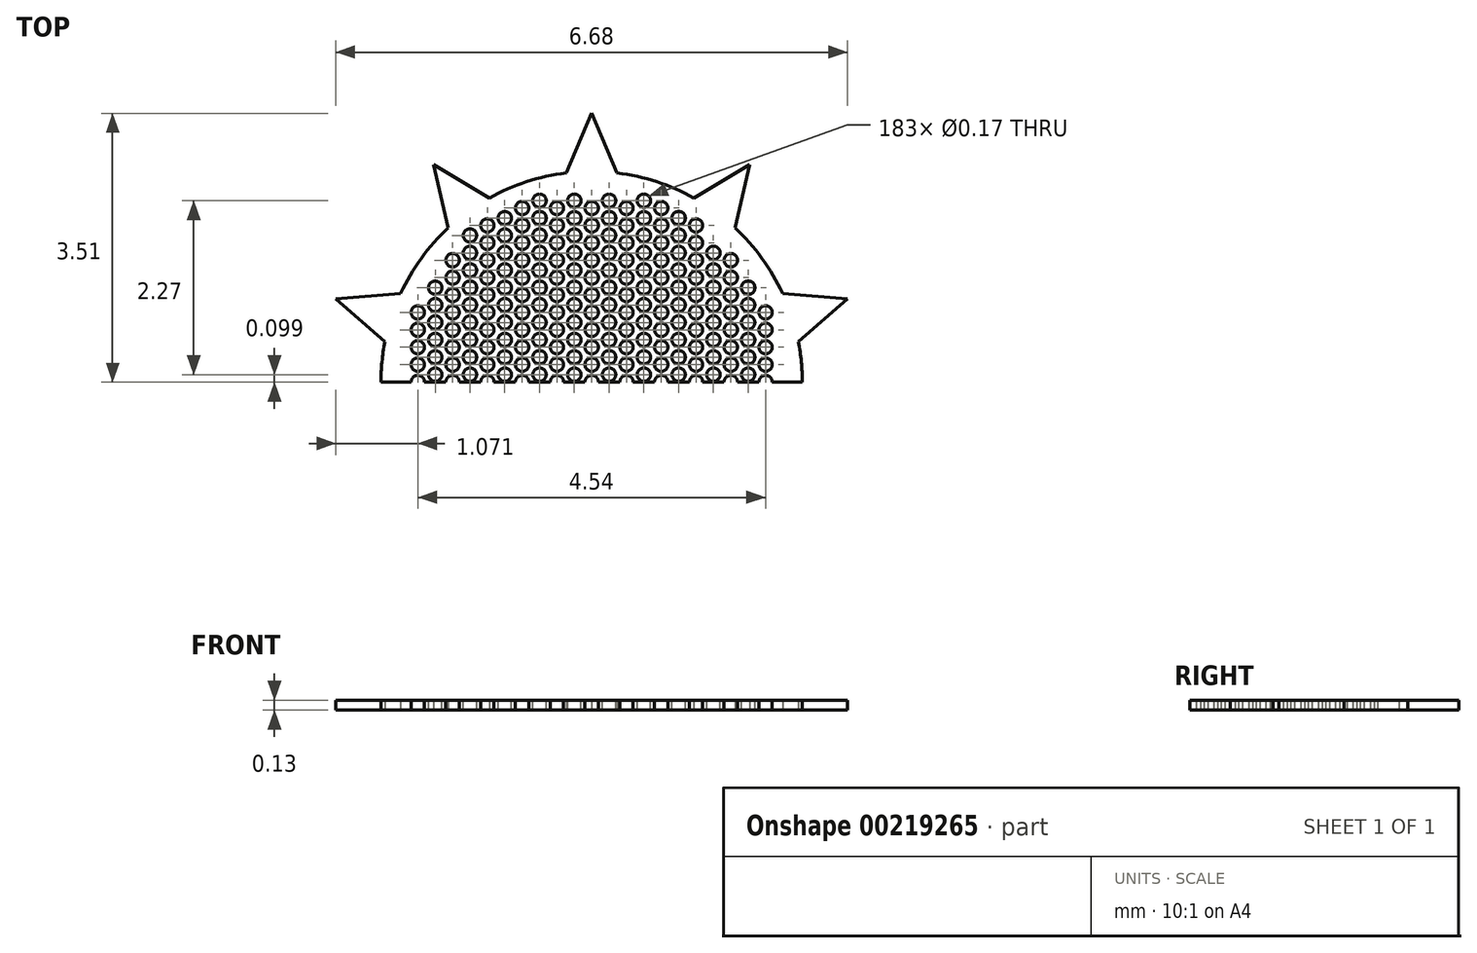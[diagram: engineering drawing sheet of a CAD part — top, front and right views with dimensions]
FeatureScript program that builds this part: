
annotation { "Feature Type Name" : "Feature", "Feature Type Description" : "" }
export const myFeature = defineFeature(function(context is Context, id is Id, definition is map)
    precondition{}
    {
        {
            var Q0;
            Q0=qCreatedBy(makeId("Top.planeOp"),FACE);
            var sketch = newSketch(context, id + "F0", { "sketchPlane" : qUnion([Q0])});
            skCircle(sketch, "E0", {"center": v(0, 0) * mm, "radius": 2.5 * mm});
            skCircle(sketch, "E1", {"center": v(0, 0) * mm, "radius": 2.75 * mm});
            skPoint(sketch, "E2", {"position": v(0, 2.75) * mm});
            skLineSegment(sketch, "E3", {"start": v(-3.94, 3.51) * mm, "end": v(3.7, 3.51) * mm, "construction": true});
            skLineSegment(sketch, "E4", {"start": v(0, 3.51) * mm, "end": v(-0.33, 2.73) * mm});
            skLineSegment(sketch, "E5", {"start": v(0, 3.51) * mm, "end": v(0.33, 2.73) * mm});
            skLineSegment(sketch, "E6.1.0", {"start": v(-2.06, 2.84) * mm, "end": v(-1.87, 2.01) * mm});
            skLineSegment(sketch, "E6.1.1", {"start": v(-2.06, 2.84) * mm, "end": v(-1.34, 2.4) * mm});
            skLineSegment(sketch, "E6.2.0", {"start": v(-3.34, 1.09) * mm, "end": v(-2.7, 0.53) * mm});
            skLineSegment(sketch, "E6.2.1", {"start": v(-3.34, 1.09) * mm, "end": v(-2.5, 1.16) * mm});
            skLineSegment(sketch, "E6.3.0", {"start": v(-3.34, -1.09) * mm, "end": v(-2.5, -1.16) * mm});
            skLineSegment(sketch, "E6.3.1", {"start": v(-3.34, -1.09) * mm, "end": v(-2.7, -0.53) * mm});
            skLineSegment(sketch, "E6.4.0", {"start": v(-2.06, -2.84) * mm, "end": v(-1.34, -2.4) * mm});
            skLineSegment(sketch, "E6.4.1", {"start": v(-2.06, -2.84) * mm, "end": v(-1.87, -2.01) * mm});
            skLineSegment(sketch, "E6.5.0", {"start": v(0, -3.51) * mm, "end": v(0.33, -2.73) * mm});
            skLineSegment(sketch, "E6.5.1", {"start": v(0, -3.51) * mm, "end": v(-0.33, -2.73) * mm});
            skLineSegment(sketch, "E6.6.0", {"start": v(2.06, -2.84) * mm, "end": v(1.87, -2.01) * mm});
            skLineSegment(sketch, "E6.6.1", {"start": v(2.06, -2.84) * mm, "end": v(1.34, -2.4) * mm});
            skLineSegment(sketch, "E6.7.0", {"start": v(3.34, -1.09) * mm, "end": v(2.7, -0.53) * mm});
            skLineSegment(sketch, "E6.7.1", {"start": v(3.34, -1.09) * mm, "end": v(2.5, -1.16) * mm});
            skLineSegment(sketch, "E6.8.0", {"start": v(3.34, 1.09) * mm, "end": v(2.5, 1.16) * mm});
            skLineSegment(sketch, "E6.8.1", {"start": v(3.34, 1.09) * mm, "end": v(2.7, 0.53) * mm});
            skLineSegment(sketch, "E6.9.0", {"start": v(2.06, 2.84) * mm, "end": v(1.34, 2.4) * mm});
            skLineSegment(sketch, "E6.9.1", {"start": v(2.06, 2.84) * mm, "end": v(1.87, 2.01) * mm});
            skSolve(sketch);
        }
        {
            var Q0;
            Q0=qSketchRegion(id+"F0",true);
            var Q1;
            Q1=makeQuery(id+"F0.imprint","IMPRINT",FACE,{"disambiguationData":[TD([[makeQuery(id+"F0.imprint","IMPRINT",EDGE,{"derivedFrom":sQuery(id+"F0.wireOp",EDGE,"E0")}),1.0]])]});
            extrude(context, id + "F1", {"entities" : qUnion([Q0, Q1]), "depth" : 0.13 * mm});
        }
        {
            var Q0;
            Q0=makeQuery(id+"F1.opExtrude","CAP_FACE",FACE,{"disambiguationData":[OSD([sQuery(id+"F0.wireOp",EDGE,"E1"),sQuery(id+"F0.wireOp",EDGE,"E4"),sQuery(id+"F0.wireOp",EDGE,"E5"),sQuery(id+"F0.wireOp",EDGE,"E6.1.0"),sQuery(id+"F0.wireOp",EDGE,"E6.1.1"),sQuery(id+"F0.wireOp",EDGE,"E6.2.0"),sQuery(id+"F0.wireOp",EDGE,"E6.2.1"),sQuery(id+"F0.wireOp",EDGE,"E6.3.0"),sQuery(id+"F0.wireOp",EDGE,"E6.3.1"),sQuery(id+"F0.wireOp",EDGE,"E6.4.0"),sQuery(id+"F0.wireOp",EDGE,"E6.4.1"),sQuery(id+"F0.wireOp",EDGE,"E6.5.0"),sQuery(id+"F0.wireOp",EDGE,"E6.5.1"),sQuery(id+"F0.wireOp",EDGE,"E6.6.0"),sQuery(id+"F0.wireOp",EDGE,"E6.6.1"),sQuery(id+"F0.wireOp",EDGE,"E6.7.0"),sQuery(id+"F0.wireOp",EDGE,"E6.7.1"),sQuery(id+"F0.wireOp",EDGE,"E6.8.0"),sQuery(id+"F0.wireOp",EDGE,"E6.8.1"),sQuery(id+"F0.wireOp",EDGE,"E6.9.0"),sQuery(id+"F0.wireOp",EDGE,"E6.9.1")])],"isStart":false});
            cPlane(context, id + "F2", {"entities" : qUnion([Q0]), "cplaneType" : CPlaneType.OFFSET, "offset" : 0 * mm, "width" : 150 * mm, "height" : 150 * mm});
        }
        {
            var Q0;
            Q0=qCreatedBy(id+"F2.planeOp",FACE);
            var sketch = newSketch(context, id + "F3", { "sketchPlane" : qUnion([Q0])});
            skCircle(sketch, "E7.2.1.8", {"center": v(-2.04, 1.23) * mm, "radius": 0.09 * mm});
            skCircle(sketch, "E7.2.1.9", {"center": v(-2.04, 1) * mm, "radius": 0.09 * mm});
            skCircle(sketch, "E7.0.1.10", {"center": v(-2.27, 0.91) * mm, "radius": 0.09 * mm});
            skCircle(sketch, "E7.2.1.10", {"center": v(-2.04, 0.78) * mm, "radius": 0.09 * mm});
            skCircle(sketch, "E7.2.2.5", {"center": v(-1.59, 1.91) * mm, "radius": 0.09 * mm});
            skCircle(sketch, "E7.2.2.6", {"center": v(-1.59, 1.69) * mm, "radius": 0.09 * mm});
            skCircle(sketch, "E7.0.2.7", {"center": v(-1.82, 1.6) * mm, "radius": 0.09 * mm});
            skCircle(sketch, "E7.2.2.7", {"center": v(-1.59, 1.46) * mm, "radius": 0.09 * mm});
            skCircle(sketch, "E7.0.2.8", {"center": v(-1.82, 1.36) * mm, "radius": 0.09 * mm});
            skCircle(sketch, "E7.2.2.8", {"center": v(-1.59, 1.23) * mm, "radius": 0.09 * mm});
            skCircle(sketch, "E7.0.2.9", {"center": v(-1.82, 1.14) * mm, "radius": 0.09 * mm});
            skCircle(sketch, "E7.2.2.9", {"center": v(-1.59, 1) * mm, "radius": 0.09 * mm});
            skCircle(sketch, "E7.0.2.10", {"center": v(-1.82, 0.91) * mm, "radius": 0.09 * mm});
            skCircle(sketch, "E7.2.2.10", {"center": v(-1.59, 0.78) * mm, "radius": 0.09 * mm});
            skCircle(sketch, "E7.2.3.4", {"center": v(-1.13, 2.14) * mm, "radius": 0.09 * mm});
            skCircle(sketch, "E7.0.3.5", {"center": v(-1.36, 2.05) * mm, "radius": 0.09 * mm});
            skCircle(sketch, "E7.2.3.5", {"center": v(-1.13, 1.91) * mm, "radius": 0.09 * mm});
            skCircle(sketch, "E7.0.3.6", {"center": v(-1.36, 1.82) * mm, "radius": 0.09 * mm});
            skCircle(sketch, "E7.2.3.6", {"center": v(-1.13, 1.69) * mm, "radius": 0.09 * mm});
            skCircle(sketch, "E7.0.3.7", {"center": v(-1.36, 1.6) * mm, "radius": 0.09 * mm});
            skCircle(sketch, "E7.2.3.7", {"center": v(-1.13, 1.46) * mm, "radius": 0.09 * mm});
            skCircle(sketch, "E7.0.3.8", {"center": v(-1.36, 1.36) * mm, "radius": 0.09 * mm});
            skCircle(sketch, "E7.2.3.8", {"center": v(-1.13, 1.23) * mm, "radius": 0.09 * mm});
            skCircle(sketch, "E7.0.3.9", {"center": v(-1.36, 1.14) * mm, "radius": 0.09 * mm});
            skCircle(sketch, "E7.2.3.9", {"center": v(-1.13, 1) * mm, "radius": 0.09 * mm});
            skCircle(sketch, "E7.0.3.10", {"center": v(-1.36, 0.91) * mm, "radius": 0.09 * mm});
            skCircle(sketch, "E7.2.3.10", {"center": v(-1.13, 0.78) * mm, "radius": 0.09 * mm});
            skCircle(sketch, "E7.2.4.3", {"center": v(-0.68, 2.37) * mm, "radius": 0.09 * mm});
            skCircle(sketch, "E7.0.4.4", {"center": v(-0.9, 2.27) * mm, "radius": 0.09 * mm});
            skCircle(sketch, "E7.2.4.4", {"center": v(-0.68, 2.14) * mm, "radius": 0.09 * mm});
            skCircle(sketch, "E7.0.4.5", {"center": v(-0.9, 2.05) * mm, "radius": 0.09 * mm});
            skCircle(sketch, "E7.2.4.5", {"center": v(-0.68, 1.91) * mm, "radius": 0.09 * mm});
            skCircle(sketch, "E7.0.4.6", {"center": v(-0.9, 1.82) * mm, "radius": 0.09 * mm});
            skCircle(sketch, "E7.2.4.6", {"center": v(-0.68, 1.69) * mm, "radius": 0.09 * mm});
            skCircle(sketch, "E7.0.4.7", {"center": v(-0.9, 1.6) * mm, "radius": 0.09 * mm});
            skCircle(sketch, "E7.2.4.7", {"center": v(-0.68, 1.46) * mm, "radius": 0.09 * mm});
            skCircle(sketch, "E7.0.4.8", {"center": v(-0.9, 1.36) * mm, "radius": 0.09 * mm});
            skCircle(sketch, "E7.2.4.8", {"center": v(-0.68, 1.23) * mm, "radius": 0.09 * mm});
            skCircle(sketch, "E7.0.4.9", {"center": v(-0.9, 1.14) * mm, "radius": 0.09 * mm});
            skCircle(sketch, "E7.2.4.9", {"center": v(-0.68, 1) * mm, "radius": 0.09 * mm});
            skCircle(sketch, "E7.0.4.10", {"center": v(-0.9, 0.91) * mm, "radius": 0.09 * mm});
            skCircle(sketch, "E7.2.4.10", {"center": v(-0.68, 0.78) * mm, "radius": 0.09 * mm});
            skCircle(sketch, "E7.2.5.3", {"center": v(-0.23, 2.37) * mm, "radius": 0.09 * mm});
            skCircle(sketch, "E7.0.5.4", {"center": v(-0.45, 2.27) * mm, "radius": 0.09 * mm});
            skCircle(sketch, "E7.2.5.4", {"center": v(-0.23, 2.14) * mm, "radius": 0.09 * mm});
            skCircle(sketch, "E7.0.5.5", {"center": v(-0.45, 2.05) * mm, "radius": 0.09 * mm});
            skCircle(sketch, "E7.2.5.5", {"center": v(-0.23, 1.91) * mm, "radius": 0.09 * mm});
            skCircle(sketch, "E7.0.5.6", {"center": v(-0.45, 1.82) * mm, "radius": 0.09 * mm});
            skCircle(sketch, "E7.2.5.6", {"center": v(-0.23, 1.69) * mm, "radius": 0.09 * mm});
            skCircle(sketch, "E7.0.5.7", {"center": v(-0.45, 1.6) * mm, "radius": 0.09 * mm});
            skCircle(sketch, "E7.2.5.7", {"center": v(-0.23, 1.46) * mm, "radius": 0.09 * mm});
            skCircle(sketch, "E7.0.5.8", {"center": v(-0.45, 1.36) * mm, "radius": 0.09 * mm});
            skCircle(sketch, "E7.2.5.8", {"center": v(-0.23, 1.23) * mm, "radius": 0.09 * mm});
            skCircle(sketch, "E7.0.5.9", {"center": v(-0.45, 1.14) * mm, "radius": 0.09 * mm});
            skCircle(sketch, "E7.2.5.9", {"center": v(-0.23, 1) * mm, "radius": 0.09 * mm});
            skCircle(sketch, "E7.0.5.10", {"center": v(-0.45, 0.91) * mm, "radius": 0.09 * mm});
            skCircle(sketch, "E7.2.5.10", {"center": v(-0.23, 0.78) * mm, "radius": 0.09 * mm});
            skCircle(sketch, "E7.2.6.3", {"center": v(0.23, 2.37) * mm, "radius": 0.09 * mm});
            skCircle(sketch, "E7.0.6.4", {"center": v(0, 2.27) * mm, "radius": 0.09 * mm});
            skCircle(sketch, "E7.2.6.4", {"center": v(0.23, 2.14) * mm, "radius": 0.09 * mm});
            skCircle(sketch, "E7.0.6.5", {"center": v(0, 2.05) * mm, "radius": 0.09 * mm});
            skCircle(sketch, "E7.2.6.5", {"center": v(0.23, 1.91) * mm, "radius": 0.09 * mm});
            skCircle(sketch, "E7.0.6.6", {"center": v(0, 1.82) * mm, "radius": 0.09 * mm});
            skCircle(sketch, "E7.2.6.6", {"center": v(0.23, 1.69) * mm, "radius": 0.09 * mm});
            skCircle(sketch, "E7.0.6.7", {"center": v(0, 1.6) * mm, "radius": 0.09 * mm});
            skCircle(sketch, "E7.2.6.7", {"center": v(0.23, 1.46) * mm, "radius": 0.09 * mm});
            skCircle(sketch, "E7.0.6.8", {"center": v(0, 1.36) * mm, "radius": 0.09 * mm});
            skCircle(sketch, "E7.2.6.8", {"center": v(0.23, 1.23) * mm, "radius": 0.09 * mm});
            skCircle(sketch, "E7.0.6.9", {"center": v(0, 1.14) * mm, "radius": 0.09 * mm});
            skCircle(sketch, "E7.2.6.9", {"center": v(0.23, 1) * mm, "radius": 0.09 * mm});
            skCircle(sketch, "E7.0.6.10", {"center": v(0, 0.91) * mm, "radius": 0.09 * mm});
            skCircle(sketch, "E7.2.6.10", {"center": v(0.23, 0.78) * mm, "radius": 0.09 * mm});
            skCircle(sketch, "E7.2.7.3", {"center": v(0.68, 2.37) * mm, "radius": 0.09 * mm});
            skCircle(sketch, "E7.0.7.4", {"center": v(0.45, 2.27) * mm, "radius": 0.09 * mm});
            skCircle(sketch, "E7.2.7.4", {"center": v(0.68, 2.14) * mm, "radius": 0.09 * mm});
            skCircle(sketch, "E7.0.7.5", {"center": v(0.45, 2.05) * mm, "radius": 0.09 * mm});
            skCircle(sketch, "E7.2.7.5", {"center": v(0.68, 1.91) * mm, "radius": 0.09 * mm});
            skCircle(sketch, "E7.0.7.6", {"center": v(0.45, 1.82) * mm, "radius": 0.09 * mm});
            skCircle(sketch, "E7.2.7.6", {"center": v(0.68, 1.69) * mm, "radius": 0.09 * mm});
            skCircle(sketch, "E7.0.7.7", {"center": v(0.45, 1.6) * mm, "radius": 0.09 * mm});
            skCircle(sketch, "E7.2.7.7", {"center": v(0.68, 1.46) * mm, "radius": 0.09 * mm});
            skCircle(sketch, "E7.0.7.8", {"center": v(0.45, 1.36) * mm, "radius": 0.09 * mm});
            skCircle(sketch, "E7.2.7.8", {"center": v(0.68, 1.23) * mm, "radius": 0.09 * mm});
            skCircle(sketch, "E7.0.7.9", {"center": v(0.45, 1.14) * mm, "radius": 0.09 * mm});
            skCircle(sketch, "E7.2.7.9", {"center": v(0.68, 1) * mm, "radius": 0.09 * mm});
            skCircle(sketch, "E7.0.7.10", {"center": v(0.45, 0.91) * mm, "radius": 0.09 * mm});
            skCircle(sketch, "E7.2.7.10", {"center": v(0.68, 0.78) * mm, "radius": 0.09 * mm});
            skCircle(sketch, "E7.0.8.4", {"center": v(0.9, 2.27) * mm, "radius": 0.09 * mm});
            skCircle(sketch, "E7.2.8.4", {"center": v(1.14, 2.14) * mm, "radius": 0.09 * mm});
            skCircle(sketch, "E7.0.8.5", {"center": v(0.9, 2.05) * mm, "radius": 0.09 * mm});
            skCircle(sketch, "E7.2.8.5", {"center": v(1.14, 1.91) * mm, "radius": 0.09 * mm});
            skCircle(sketch, "E7.0.8.6", {"center": v(0.9, 1.82) * mm, "radius": 0.09 * mm});
            skCircle(sketch, "E7.2.8.6", {"center": v(1.14, 1.69) * mm, "radius": 0.09 * mm});
            skCircle(sketch, "E7.0.8.7", {"center": v(0.9, 1.6) * mm, "radius": 0.09 * mm});
            skCircle(sketch, "E7.2.8.7", {"center": v(1.14, 1.46) * mm, "radius": 0.09 * mm});
            skCircle(sketch, "E7.0.8.8", {"center": v(0.9, 1.36) * mm, "radius": 0.09 * mm});
            skCircle(sketch, "E7.2.8.8", {"center": v(1.14, 1.23) * mm, "radius": 0.09 * mm});
            skCircle(sketch, "E7.0.8.9", {"center": v(0.9, 1.14) * mm, "radius": 0.09 * mm});
            skCircle(sketch, "E7.2.8.9", {"center": v(1.14, 1) * mm, "radius": 0.09 * mm});
            skCircle(sketch, "E7.0.8.10", {"center": v(0.9, 0.91) * mm, "radius": 0.09 * mm});
            skCircle(sketch, "E7.2.8.10", {"center": v(1.14, 0.78) * mm, "radius": 0.09 * mm});
            skCircle(sketch, "E7.0.9.5", {"center": v(1.36, 2.05) * mm, "radius": 0.09 * mm});
            skCircle(sketch, "E7.0.9.6", {"center": v(1.36, 1.82) * mm, "radius": 0.09 * mm});
            skCircle(sketch, "E7.2.9.6", {"center": v(1.6, 1.69) * mm, "radius": 0.09 * mm});
            skCircle(sketch, "E7.0.9.7", {"center": v(1.36, 1.6) * mm, "radius": 0.09 * mm});
            skCircle(sketch, "E7.2.9.7", {"center": v(1.6, 1.46) * mm, "radius": 0.09 * mm});
            skCircle(sketch, "E7.0.9.8", {"center": v(1.36, 1.36) * mm, "radius": 0.09 * mm});
            skCircle(sketch, "E7.2.9.8", {"center": v(1.6, 1.23) * mm, "radius": 0.09 * mm});
            skCircle(sketch, "E7.0.9.9", {"center": v(1.36, 1.14) * mm, "radius": 0.09 * mm});
            skCircle(sketch, "E7.2.9.9", {"center": v(1.6, 1) * mm, "radius": 0.09 * mm});
            skCircle(sketch, "E7.0.9.10", {"center": v(1.36, 0.91) * mm, "radius": 0.09 * mm});
            skCircle(sketch, "E7.2.9.10", {"center": v(1.6, 0.78) * mm, "radius": 0.09 * mm});
            skCircle(sketch, "E7.0.10.7", {"center": v(1.82, 1.6) * mm, "radius": 0.09 * mm});
            skCircle(sketch, "E7.0.10.8", {"center": v(1.82, 1.36) * mm, "radius": 0.09 * mm});
            skCircle(sketch, "E7.2.10.8", {"center": v(2.04, 1.23) * mm, "radius": 0.09 * mm});
            skCircle(sketch, "E7.0.10.9", {"center": v(1.82, 1.14) * mm, "radius": 0.09 * mm});
            skCircle(sketch, "E7.2.10.9", {"center": v(2.04, 1) * mm, "radius": 0.09 * mm});
            skCircle(sketch, "E7.0.10.10", {"center": v(1.82, 0.91) * mm, "radius": 0.09 * mm});
            skCircle(sketch, "E7.2.10.10", {"center": v(2.04, 0.78) * mm, "radius": 0.09 * mm});
            skCircle(sketch, "E8.0.1.11", {"center": v(-2.27, 0.68) * mm, "radius": 0.09 * mm});
            skCircle(sketch, "E8.2.1.11", {"center": v(-2.04, 0.55) * mm, "radius": 0.09 * mm});
            skCircle(sketch, "E8.0.1.12", {"center": v(-2.27, 0.46) * mm, "radius": 0.09 * mm});
            skCircle(sketch, "E8.2.1.12", {"center": v(-2.04, 0.33) * mm, "radius": 0.09 * mm});
            skCircle(sketch, "E8.0.1.13", {"center": v(-2.27, 0.23) * mm, "radius": 0.09 * mm});
            skCircle(sketch, "E8.2.1.13", {"center": v(-2.04, 0.1) * mm, "radius": 0.09 * mm});
            skCircle(sketch, "E8.0.1.14", {"center": v(-2.27, 0) * mm, "radius": 0.09 * mm});
            skCircle(sketch, "E8.2.1.14", {"center": v(-2.04, -0.13) * mm, "radius": 0.09 * mm});
            skCircle(sketch, "E8.0.1.15", {"center": v(-2.27, -0.22) * mm, "radius": 0.09 * mm});
            skCircle(sketch, "E8.2.1.15", {"center": v(-2.04, -0.36) * mm, "radius": 0.09 * mm});
            skCircle(sketch, "E8.0.1.16", {"center": v(-2.27, -0.45) * mm, "radius": 0.09 * mm});
            skCircle(sketch, "E8.2.1.16", {"center": v(-2.04, -0.58) * mm, "radius": 0.09 * mm});
            skCircle(sketch, "E8.0.1.17", {"center": v(-2.27, -0.68) * mm, "radius": 0.09 * mm});
            skCircle(sketch, "E8.2.1.17", {"center": v(-2.04, -0.8) * mm, "radius": 0.09 * mm});
            skCircle(sketch, "E8.0.1.18", {"center": v(-2.27, -0.9) * mm, "radius": 0.09 * mm});
            skCircle(sketch, "E8.2.1.18", {"center": v(-2.04, -1.04) * mm, "radius": 0.09 * mm});
            skCircle(sketch, "E8.2.1.19", {"center": v(-2.04, -1.26) * mm, "radius": 0.09 * mm});
            skCircle(sketch, "E8.0.2.11", {"center": v(-1.82, 0.68) * mm, "radius": 0.09 * mm});
            skCircle(sketch, "E8.2.2.11", {"center": v(-1.59, 0.55) * mm, "radius": 0.09 * mm});
            skCircle(sketch, "E8.0.2.12", {"center": v(-1.82, 0.46) * mm, "radius": 0.09 * mm});
            skCircle(sketch, "E8.2.2.12", {"center": v(-1.59, 0.33) * mm, "radius": 0.09 * mm});
            skCircle(sketch, "E8.0.2.13", {"center": v(-1.82, 0.23) * mm, "radius": 0.09 * mm});
            skCircle(sketch, "E8.2.2.13", {"center": v(-1.59, 0.1) * mm, "radius": 0.09 * mm});
            skCircle(sketch, "E8.0.2.14", {"center": v(-1.82, 0) * mm, "radius": 0.09 * mm});
            skCircle(sketch, "E8.2.2.14", {"center": v(-1.59, -0.13) * mm, "radius": 0.09 * mm});
            skCircle(sketch, "E8.0.2.15", {"center": v(-1.82, -0.22) * mm, "radius": 0.09 * mm});
            skCircle(sketch, "E8.2.2.15", {"center": v(-1.59, -0.36) * mm, "radius": 0.09 * mm});
            skCircle(sketch, "E8.0.2.16", {"center": v(-1.82, -0.45) * mm, "radius": 0.09 * mm});
            skCircle(sketch, "E8.2.2.16", {"center": v(-1.59, -0.58) * mm, "radius": 0.09 * mm});
            skCircle(sketch, "E8.0.2.17", {"center": v(-1.82, -0.68) * mm, "radius": 0.09 * mm});
            skCircle(sketch, "E8.2.2.17", {"center": v(-1.59, -0.8) * mm, "radius": 0.09 * mm});
            skCircle(sketch, "E8.0.2.18", {"center": v(-1.82, -0.9) * mm, "radius": 0.09 * mm});
            skCircle(sketch, "E8.2.2.18", {"center": v(-1.59, -1.04) * mm, "radius": 0.09 * mm});
            skCircle(sketch, "E8.0.2.19", {"center": v(-1.82, -1.13) * mm, "radius": 0.09 * mm});
            skCircle(sketch, "E8.2.2.19", {"center": v(-1.59, -1.26) * mm, "radius": 0.09 * mm});
            skCircle(sketch, "E8.0.2.20", {"center": v(-1.82, -1.36) * mm, "radius": 0.09 * mm});
            skCircle(sketch, "E8.2.2.20", {"center": v(-1.59, -1.5) * mm, "radius": 0.09 * mm});
            skCircle(sketch, "E8.0.2.21", {"center": v(-1.82, -1.59) * mm, "radius": 0.09 * mm});
            skCircle(sketch, "E8.2.2.21", {"center": v(-1.59, -1.72) * mm, "radius": 0.09 * mm});
            skCircle(sketch, "E8.0.3.11", {"center": v(-1.36, 0.68) * mm, "radius": 0.09 * mm});
            skCircle(sketch, "E8.2.3.11", {"center": v(-1.13, 0.55) * mm, "radius": 0.09 * mm});
            skCircle(sketch, "E8.0.3.12", {"center": v(-1.36, 0.46) * mm, "radius": 0.09 * mm});
            skCircle(sketch, "E8.2.3.12", {"center": v(-1.13, 0.33) * mm, "radius": 0.09 * mm});
            skCircle(sketch, "E8.0.3.13", {"center": v(-1.36, 0.23) * mm, "radius": 0.09 * mm});
            skCircle(sketch, "E8.2.3.13", {"center": v(-1.13, 0.1) * mm, "radius": 0.09 * mm});
            skCircle(sketch, "E8.0.3.14", {"center": v(-1.36, 0) * mm, "radius": 0.09 * mm});
            skCircle(sketch, "E8.2.3.14", {"center": v(-1.13, -0.13) * mm, "radius": 0.09 * mm});
            skCircle(sketch, "E8.0.3.15", {"center": v(-1.36, -0.22) * mm, "radius": 0.09 * mm});
            skCircle(sketch, "E8.2.3.15", {"center": v(-1.13, -0.36) * mm, "radius": 0.09 * mm});
            skCircle(sketch, "E8.0.3.16", {"center": v(-1.36, -0.45) * mm, "radius": 0.09 * mm});
            skCircle(sketch, "E8.2.3.16", {"center": v(-1.13, -0.58) * mm, "radius": 0.09 * mm});
            skCircle(sketch, "E8.0.3.17", {"center": v(-1.36, -0.68) * mm, "radius": 0.09 * mm});
            skCircle(sketch, "E8.2.3.17", {"center": v(-1.13, -0.8) * mm, "radius": 0.09 * mm});
            skCircle(sketch, "E8.0.3.18", {"center": v(-1.36, -0.9) * mm, "radius": 0.09 * mm});
            skCircle(sketch, "E8.2.3.18", {"center": v(-1.13, -1.04) * mm, "radius": 0.09 * mm});
            skCircle(sketch, "E8.0.3.19", {"center": v(-1.36, -1.13) * mm, "radius": 0.09 * mm});
            skCircle(sketch, "E8.2.3.19", {"center": v(-1.13, -1.26) * mm, "radius": 0.09 * mm});
            skCircle(sketch, "E8.0.3.20", {"center": v(-1.36, -1.36) * mm, "radius": 0.09 * mm});
            skCircle(sketch, "E8.2.3.20", {"center": v(-1.13, -1.5) * mm, "radius": 0.09 * mm});
            skCircle(sketch, "E8.0.3.21", {"center": v(-1.36, -1.59) * mm, "radius": 0.09 * mm});
            skCircle(sketch, "E8.2.3.21", {"center": v(-1.13, -1.72) * mm, "radius": 0.09 * mm});
            skCircle(sketch, "E8.0.4.11", {"center": v(-0.9, 0.68) * mm, "radius": 0.09 * mm});
            skCircle(sketch, "E8.2.4.11", {"center": v(-0.68, 0.55) * mm, "radius": 0.09 * mm});
            skCircle(sketch, "E8.0.4.12", {"center": v(-0.9, 0.46) * mm, "radius": 0.09 * mm});
            skCircle(sketch, "E8.2.4.12", {"center": v(-0.68, 0.33) * mm, "radius": 0.09 * mm});
            skCircle(sketch, "E8.0.4.13", {"center": v(-0.9, 0.23) * mm, "radius": 0.09 * mm});
            skCircle(sketch, "E8.2.4.13", {"center": v(-0.68, 0.1) * mm, "radius": 0.09 * mm});
            skCircle(sketch, "E8.0.4.14", {"center": v(-0.9, 0) * mm, "radius": 0.09 * mm});
            skCircle(sketch, "E8.2.4.14", {"center": v(-0.68, -0.13) * mm, "radius": 0.09 * mm});
            skCircle(sketch, "E8.0.4.15", {"center": v(-0.9, -0.22) * mm, "radius": 0.09 * mm});
            skCircle(sketch, "E8.2.4.15", {"center": v(-0.68, -0.36) * mm, "radius": 0.09 * mm});
            skCircle(sketch, "E8.0.4.16", {"center": v(-0.9, -0.45) * mm, "radius": 0.09 * mm});
            skCircle(sketch, "E8.2.4.16", {"center": v(-0.68, -0.58) * mm, "radius": 0.09 * mm});
            skCircle(sketch, "E8.0.4.17", {"center": v(-0.9, -0.68) * mm, "radius": 0.09 * mm});
            skCircle(sketch, "E8.2.4.17", {"center": v(-0.68, -0.8) * mm, "radius": 0.09 * mm});
            skCircle(sketch, "E8.0.4.18", {"center": v(-0.9, -0.9) * mm, "radius": 0.09 * mm});
            skCircle(sketch, "E8.2.4.18", {"center": v(-0.68, -1.04) * mm, "radius": 0.09 * mm});
            skCircle(sketch, "E8.0.4.19", {"center": v(-0.9, -1.13) * mm, "radius": 0.09 * mm});
            skCircle(sketch, "E8.2.4.19", {"center": v(-0.68, -1.26) * mm, "radius": 0.09 * mm});
            skCircle(sketch, "E8.0.4.20", {"center": v(-0.9, -1.36) * mm, "radius": 0.09 * mm});
            skCircle(sketch, "E8.2.4.20", {"center": v(-0.68, -1.5) * mm, "radius": 0.09 * mm});
            skCircle(sketch, "E8.0.4.21", {"center": v(-0.9, -1.59) * mm, "radius": 0.09 * mm});
            skCircle(sketch, "E8.2.4.21", {"center": v(-0.68, -1.72) * mm, "radius": 0.09 * mm});
            skCircle(sketch, "E8.0.5.11", {"center": v(-0.45, 0.68) * mm, "radius": 0.09 * mm});
            skCircle(sketch, "E8.2.5.11", {"center": v(-0.23, 0.55) * mm, "radius": 0.09 * mm});
            skCircle(sketch, "E8.0.5.12", {"center": v(-0.45, 0.46) * mm, "radius": 0.09 * mm});
            skCircle(sketch, "E8.2.5.12", {"center": v(-0.23, 0.33) * mm, "radius": 0.09 * mm});
            skCircle(sketch, "E8.0.5.13", {"center": v(-0.45, 0.23) * mm, "radius": 0.09 * mm});
            skCircle(sketch, "E8.2.5.13", {"center": v(-0.23, 0.1) * mm, "radius": 0.09 * mm});
            skCircle(sketch, "E8.0.5.14", {"center": v(-0.45, 0) * mm, "radius": 0.09 * mm});
            skCircle(sketch, "E8.2.5.14", {"center": v(-0.23, -0.13) * mm, "radius": 0.09 * mm});
            skCircle(sketch, "E8.0.5.15", {"center": v(-0.45, -0.22) * mm, "radius": 0.09 * mm});
            skCircle(sketch, "E8.2.5.15", {"center": v(-0.23, -0.36) * mm, "radius": 0.09 * mm});
            skCircle(sketch, "E8.0.5.16", {"center": v(-0.45, -0.45) * mm, "radius": 0.09 * mm});
            skCircle(sketch, "E8.2.5.16", {"center": v(-0.23, -0.58) * mm, "radius": 0.09 * mm});
            skCircle(sketch, "E8.0.5.17", {"center": v(-0.45, -0.68) * mm, "radius": 0.09 * mm});
            skCircle(sketch, "E8.2.5.17", {"center": v(-0.23, -0.8) * mm, "radius": 0.09 * mm});
            skCircle(sketch, "E8.0.5.18", {"center": v(-0.45, -0.9) * mm, "radius": 0.09 * mm});
            skCircle(sketch, "E8.2.5.18", {"center": v(-0.23, -1.04) * mm, "radius": 0.09 * mm});
            skCircle(sketch, "E8.0.5.19", {"center": v(-0.45, -1.13) * mm, "radius": 0.09 * mm});
            skCircle(sketch, "E8.2.5.19", {"center": v(-0.23, -1.26) * mm, "radius": 0.09 * mm});
            skCircle(sketch, "E8.0.5.20", {"center": v(-0.45, -1.36) * mm, "radius": 0.09 * mm});
            skCircle(sketch, "E8.2.5.20", {"center": v(-0.23, -1.5) * mm, "radius": 0.09 * mm});
            skCircle(sketch, "E8.0.5.21", {"center": v(-0.45, -1.59) * mm, "radius": 0.09 * mm});
            skCircle(sketch, "E8.2.5.21", {"center": v(-0.23, -1.72) * mm, "radius": 0.09 * mm});
            skCircle(sketch, "E8.0.6.11", {"center": v(0, 0.68) * mm, "radius": 0.09 * mm});
            skCircle(sketch, "E8.2.6.11", {"center": v(0.23, 0.55) * mm, "radius": 0.09 * mm});
            skCircle(sketch, "E8.0.6.12", {"center": v(0, 0.46) * mm, "radius": 0.09 * mm});
            skCircle(sketch, "E8.2.6.12", {"center": v(0.23, 0.33) * mm, "radius": 0.09 * mm});
            skCircle(sketch, "E8.0.6.13", {"center": v(0, 0.23) * mm, "radius": 0.09 * mm});
            skCircle(sketch, "E8.2.6.13", {"center": v(0.23, 0.1) * mm, "radius": 0.09 * mm});
            skCircle(sketch, "E8.0.6.14", {"center": v(0, 0) * mm, "radius": 0.09 * mm});
            skCircle(sketch, "E8.2.6.14", {"center": v(0.23, -0.13) * mm, "radius": 0.09 * mm});
            skCircle(sketch, "E8.0.6.15", {"center": v(0, -0.22) * mm, "radius": 0.09 * mm});
            skCircle(sketch, "E8.2.6.15", {"center": v(0.23, -0.36) * mm, "radius": 0.09 * mm});
            skCircle(sketch, "E8.0.6.16", {"center": v(0, -0.45) * mm, "radius": 0.09 * mm});
            skCircle(sketch, "E8.2.6.16", {"center": v(0.23, -0.58) * mm, "radius": 0.09 * mm});
            skCircle(sketch, "E8.0.6.17", {"center": v(0, -0.68) * mm, "radius": 0.09 * mm});
            skCircle(sketch, "E8.2.6.17", {"center": v(0.23, -0.8) * mm, "radius": 0.09 * mm});
            skCircle(sketch, "E8.0.6.18", {"center": v(0, -0.9) * mm, "radius": 0.09 * mm});
            skCircle(sketch, "E8.2.6.18", {"center": v(0.23, -1.04) * mm, "radius": 0.09 * mm});
            skCircle(sketch, "E8.0.6.19", {"center": v(0, -1.13) * mm, "radius": 0.09 * mm});
            skCircle(sketch, "E8.2.6.19", {"center": v(0.23, -1.26) * mm, "radius": 0.09 * mm});
            skCircle(sketch, "E8.0.6.20", {"center": v(0, -1.36) * mm, "radius": 0.09 * mm});
            skCircle(sketch, "E8.2.6.20", {"center": v(0.23, -1.5) * mm, "radius": 0.09 * mm});
            skCircle(sketch, "E8.0.6.21", {"center": v(0, -1.59) * mm, "radius": 0.09 * mm});
            skCircle(sketch, "E8.2.6.21", {"center": v(0.23, -1.72) * mm, "radius": 0.09 * mm});
            skCircle(sketch, "E8.0.7.11", {"center": v(0.45, 0.68) * mm, "radius": 0.09 * mm});
            skCircle(sketch, "E8.2.7.11", {"center": v(0.68, 0.55) * mm, "radius": 0.09 * mm});
            skCircle(sketch, "E8.0.7.12", {"center": v(0.45, 0.46) * mm, "radius": 0.09 * mm});
            skCircle(sketch, "E8.2.7.12", {"center": v(0.68, 0.33) * mm, "radius": 0.09 * mm});
            skCircle(sketch, "E8.0.7.13", {"center": v(0.45, 0.23) * mm, "radius": 0.09 * mm});
            skCircle(sketch, "E8.2.7.13", {"center": v(0.68, 0.1) * mm, "radius": 0.09 * mm});
            skCircle(sketch, "E8.0.7.14", {"center": v(0.45, 0) * mm, "radius": 0.09 * mm});
            skCircle(sketch, "E8.2.7.14", {"center": v(0.68, -0.13) * mm, "radius": 0.09 * mm});
            skCircle(sketch, "E8.0.7.15", {"center": v(0.45, -0.22) * mm, "radius": 0.09 * mm});
            skCircle(sketch, "E8.2.7.15", {"center": v(0.68, -0.36) * mm, "radius": 0.09 * mm});
            skCircle(sketch, "E8.0.7.16", {"center": v(0.45, -0.45) * mm, "radius": 0.09 * mm});
            skCircle(sketch, "E8.2.7.16", {"center": v(0.68, -0.58) * mm, "radius": 0.09 * mm});
            skCircle(sketch, "E8.0.7.17", {"center": v(0.45, -0.68) * mm, "radius": 0.09 * mm});
            skCircle(sketch, "E8.2.7.17", {"center": v(0.68, -0.8) * mm, "radius": 0.09 * mm});
            skCircle(sketch, "E8.0.7.18", {"center": v(0.45, -0.9) * mm, "radius": 0.09 * mm});
            skCircle(sketch, "E8.2.7.18", {"center": v(0.68, -1.04) * mm, "radius": 0.09 * mm});
            skCircle(sketch, "E8.0.7.19", {"center": v(0.45, -1.13) * mm, "radius": 0.09 * mm});
            skCircle(sketch, "E8.2.7.19", {"center": v(0.68, -1.26) * mm, "radius": 0.09 * mm});
            skCircle(sketch, "E8.0.7.20", {"center": v(0.45, -1.36) * mm, "radius": 0.09 * mm});
            skCircle(sketch, "E8.2.7.20", {"center": v(0.68, -1.5) * mm, "radius": 0.09 * mm});
            skCircle(sketch, "E8.0.7.21", {"center": v(0.45, -1.59) * mm, "radius": 0.09 * mm});
            skCircle(sketch, "E8.2.7.21", {"center": v(0.68, -1.72) * mm, "radius": 0.09 * mm});
            skCircle(sketch, "E8.0.8.11", {"center": v(0.9, 0.68) * mm, "radius": 0.09 * mm});
            skCircle(sketch, "E8.2.8.11", {"center": v(1.14, 0.55) * mm, "radius": 0.09 * mm});
            skCircle(sketch, "E8.0.8.12", {"center": v(0.9, 0.46) * mm, "radius": 0.09 * mm});
            skCircle(sketch, "E8.2.8.12", {"center": v(1.14, 0.33) * mm, "radius": 0.09 * mm});
            skCircle(sketch, "E8.0.8.13", {"center": v(0.9, 0.23) * mm, "radius": 0.09 * mm});
            skCircle(sketch, "E8.2.8.13", {"center": v(1.14, 0.1) * mm, "radius": 0.09 * mm});
            skCircle(sketch, "E8.0.8.14", {"center": v(0.9, 0) * mm, "radius": 0.09 * mm});
            skCircle(sketch, "E8.2.8.14", {"center": v(1.14, -0.13) * mm, "radius": 0.09 * mm});
            skCircle(sketch, "E8.0.8.15", {"center": v(0.9, -0.22) * mm, "radius": 0.09 * mm});
            skCircle(sketch, "E8.2.8.15", {"center": v(1.14, -0.36) * mm, "radius": 0.09 * mm});
            skCircle(sketch, "E8.0.8.16", {"center": v(0.9, -0.45) * mm, "radius": 0.09 * mm});
            skCircle(sketch, "E8.2.8.16", {"center": v(1.14, -0.58) * mm, "radius": 0.09 * mm});
            skCircle(sketch, "E8.0.8.17", {"center": v(0.9, -0.68) * mm, "radius": 0.09 * mm});
            skCircle(sketch, "E8.2.8.17", {"center": v(1.14, -0.8) * mm, "radius": 0.09 * mm});
            skCircle(sketch, "E8.0.8.18", {"center": v(0.9, -0.9) * mm, "radius": 0.09 * mm});
            skCircle(sketch, "E8.2.8.18", {"center": v(1.14, -1.04) * mm, "radius": 0.09 * mm});
            skCircle(sketch, "E8.0.8.19", {"center": v(0.9, -1.13) * mm, "radius": 0.09 * mm});
            skCircle(sketch, "E8.2.8.19", {"center": v(1.14, -1.26) * mm, "radius": 0.09 * mm});
            skCircle(sketch, "E8.0.8.20", {"center": v(0.9, -1.36) * mm, "radius": 0.09 * mm});
            skCircle(sketch, "E8.2.8.20", {"center": v(1.14, -1.5) * mm, "radius": 0.09 * mm});
            skCircle(sketch, "E8.0.8.21", {"center": v(0.9, -1.59) * mm, "radius": 0.09 * mm});
            skCircle(sketch, "E8.2.8.21", {"center": v(1.14, -1.72) * mm, "radius": 0.09 * mm});
            skCircle(sketch, "E8.0.9.11", {"center": v(1.36, 0.68) * mm, "radius": 0.09 * mm});
            skCircle(sketch, "E8.2.9.11", {"center": v(1.6, 0.55) * mm, "radius": 0.09 * mm});
            skCircle(sketch, "E8.0.9.12", {"center": v(1.36, 0.46) * mm, "radius": 0.09 * mm});
            skCircle(sketch, "E8.2.9.12", {"center": v(1.6, 0.33) * mm, "radius": 0.09 * mm});
            skCircle(sketch, "E8.0.9.13", {"center": v(1.36, 0.23) * mm, "radius": 0.09 * mm});
            skCircle(sketch, "E8.2.9.13", {"center": v(1.6, 0.1) * mm, "radius": 0.09 * mm});
            skCircle(sketch, "E8.0.9.14", {"center": v(1.36, 0) * mm, "radius": 0.09 * mm});
            skCircle(sketch, "E8.2.9.14", {"center": v(1.6, -0.13) * mm, "radius": 0.09 * mm});
            skCircle(sketch, "E8.0.9.15", {"center": v(1.36, -0.22) * mm, "radius": 0.09 * mm});
            skCircle(sketch, "E8.2.9.15", {"center": v(1.6, -0.36) * mm, "radius": 0.09 * mm});
            skCircle(sketch, "E8.0.9.16", {"center": v(1.36, -0.45) * mm, "radius": 0.09 * mm});
            skCircle(sketch, "E8.2.9.16", {"center": v(1.6, -0.58) * mm, "radius": 0.09 * mm});
            skCircle(sketch, "E8.0.9.17", {"center": v(1.36, -0.68) * mm, "radius": 0.09 * mm});
            skCircle(sketch, "E8.2.9.17", {"center": v(1.6, -0.8) * mm, "radius": 0.09 * mm});
            skCircle(sketch, "E8.0.9.18", {"center": v(1.36, -0.9) * mm, "radius": 0.09 * mm});
            skCircle(sketch, "E8.2.9.18", {"center": v(1.6, -1.04) * mm, "radius": 0.09 * mm});
            skCircle(sketch, "E8.0.9.19", {"center": v(1.36, -1.13) * mm, "radius": 0.09 * mm});
            skCircle(sketch, "E8.2.9.19", {"center": v(1.6, -1.26) * mm, "radius": 0.09 * mm});
            skCircle(sketch, "E8.0.9.20", {"center": v(1.36, -1.36) * mm, "radius": 0.09 * mm});
            skCircle(sketch, "E8.2.9.20", {"center": v(1.6, -1.5) * mm, "radius": 0.09 * mm});
            skCircle(sketch, "E8.0.9.21", {"center": v(1.36, -1.59) * mm, "radius": 0.09 * mm});
            skCircle(sketch, "E8.2.9.21", {"center": v(1.6, -1.72) * mm, "radius": 0.09 * mm});
            skCircle(sketch, "E8.0.10.11", {"center": v(1.82, 0.68) * mm, "radius": 0.09 * mm});
            skCircle(sketch, "E8.2.10.11", {"center": v(2.04, 0.55) * mm, "radius": 0.09 * mm});
            skCircle(sketch, "E8.0.10.12", {"center": v(1.82, 0.46) * mm, "radius": 0.09 * mm});
            skCircle(sketch, "E8.2.10.12", {"center": v(2.04, 0.33) * mm, "radius": 0.09 * mm});
            skCircle(sketch, "E8.0.10.13", {"center": v(1.82, 0.23) * mm, "radius": 0.09 * mm});
            skCircle(sketch, "E8.2.10.13", {"center": v(2.04, 0.1) * mm, "radius": 0.09 * mm});
            skCircle(sketch, "E8.0.10.14", {"center": v(1.82, 0) * mm, "radius": 0.09 * mm});
            skCircle(sketch, "E8.2.10.14", {"center": v(2.04, -0.13) * mm, "radius": 0.09 * mm});
            skCircle(sketch, "E8.0.10.15", {"center": v(1.82, -0.22) * mm, "radius": 0.09 * mm});
            skCircle(sketch, "E8.2.10.15", {"center": v(2.04, -0.36) * mm, "radius": 0.09 * mm});
            skCircle(sketch, "E8.0.10.16", {"center": v(1.82, -0.45) * mm, "radius": 0.09 * mm});
            skCircle(sketch, "E8.2.10.16", {"center": v(2.04, -0.58) * mm, "radius": 0.09 * mm});
            skCircle(sketch, "E8.0.10.17", {"center": v(1.82, -0.68) * mm, "radius": 0.09 * mm});
            skCircle(sketch, "E8.2.10.17", {"center": v(2.04, -0.8) * mm, "radius": 0.09 * mm});
            skCircle(sketch, "E8.0.10.18", {"center": v(1.82, -0.9) * mm, "radius": 0.09 * mm});
            skCircle(sketch, "E8.2.10.18", {"center": v(2.04, -1.04) * mm, "radius": 0.09 * mm});
            skCircle(sketch, "E8.0.10.19", {"center": v(1.82, -1.13) * mm, "radius": 0.09 * mm});
            skCircle(sketch, "E8.2.10.19", {"center": v(2.04, -1.26) * mm, "radius": 0.09 * mm});
            skCircle(sketch, "E8.0.10.20", {"center": v(1.82, -1.36) * mm, "radius": 0.09 * mm});
            skCircle(sketch, "E8.0.10.21", {"center": v(1.82, -1.59) * mm, "radius": 0.09 * mm});
            skCircle(sketch, "E9.0.11.10", {"center": v(2.27, 0.91) * mm, "radius": 0.09 * mm});
            skCircle(sketch, "E9.0.11.11", {"center": v(2.27, 0.68) * mm, "radius": 0.09 * mm});
            skCircle(sketch, "E9.0.11.12", {"center": v(2.27, 0.46) * mm, "radius": 0.09 * mm});
            skCircle(sketch, "E9.0.11.13", {"center": v(2.27, 0.23) * mm, "radius": 0.09 * mm});
            skCircle(sketch, "E9.0.11.14", {"center": v(2.27, 0) * mm, "radius": 0.09 * mm});
            skCircle(sketch, "E9.0.11.15", {"center": v(2.27, -0.22) * mm, "radius": 0.09 * mm});
            skCircle(sketch, "E9.0.11.16", {"center": v(2.27, -0.45) * mm, "radius": 0.09 * mm});
            skCircle(sketch, "E9.0.11.17", {"center": v(2.27, -0.68) * mm, "radius": 0.09 * mm});
            skCircle(sketch, "E9.0.11.18", {"center": v(2.27, -0.9) * mm, "radius": 0.09 * mm});
            skCircle(sketch, "E10.0.3.22", {"center": v(-1.36, -1.81) * mm, "radius": 0.09 * mm});
            skCircle(sketch, "E10.2.3.22", {"center": v(-1.13, -1.94) * mm, "radius": 0.09 * mm});
            skCircle(sketch, "E10.0.3.23", {"center": v(-1.36, -2.04) * mm, "radius": 0.09 * mm});
            skCircle(sketch, "E10.2.3.23", {"center": v(-1.13, -2.17) * mm, "radius": 0.09 * mm});
            skCircle(sketch, "E10.0.4.22", {"center": v(-0.9, -1.81) * mm, "radius": 0.09 * mm});
            skCircle(sketch, "E10.2.4.22", {"center": v(-0.68, -1.94) * mm, "radius": 0.09 * mm});
            skCircle(sketch, "E10.0.4.23", {"center": v(-0.9, -2.04) * mm, "radius": 0.09 * mm});
            skCircle(sketch, "E10.2.4.23", {"center": v(-0.68, -2.17) * mm, "radius": 0.09 * mm});
            skCircle(sketch, "E10.0.4.24", {"center": v(-0.9, -2.27) * mm, "radius": 0.09 * mm});
            skCircle(sketch, "E10.0.5.22", {"center": v(-0.45, -1.81) * mm, "radius": 0.09 * mm});
            skCircle(sketch, "E10.2.5.22", {"center": v(-0.23, -1.94) * mm, "radius": 0.09 * mm});
            skCircle(sketch, "E10.0.5.23", {"center": v(-0.45, -2.04) * mm, "radius": 0.09 * mm});
            skCircle(sketch, "E10.2.5.23", {"center": v(-0.23, -2.17) * mm, "radius": 0.09 * mm});
            skCircle(sketch, "E10.0.5.24", {"center": v(-0.45, -2.27) * mm, "radius": 0.09 * mm});
            skCircle(sketch, "E10.2.5.24", {"center": v(-0.23, -2.4) * mm, "radius": 0.09 * mm});
            skCircle(sketch, "E10.0.6.22", {"center": v(0, -1.81) * mm, "radius": 0.09 * mm});
            skCircle(sketch, "E10.2.6.22", {"center": v(0.23, -1.94) * mm, "radius": 0.09 * mm});
            skCircle(sketch, "E10.0.6.23", {"center": v(0, -2.04) * mm, "radius": 0.09 * mm});
            skCircle(sketch, "E10.2.6.23", {"center": v(0.23, -2.17) * mm, "radius": 0.09 * mm});
            skCircle(sketch, "E10.0.6.24", {"center": v(0, -2.27) * mm, "radius": 0.09 * mm});
            skCircle(sketch, "E10.2.6.24", {"center": v(0.23, -2.4) * mm, "radius": 0.09 * mm});
            skCircle(sketch, "E10.0.7.22", {"center": v(0.45, -1.81) * mm, "radius": 0.09 * mm});
            skCircle(sketch, "E10.2.7.22", {"center": v(0.68, -1.94) * mm, "radius": 0.09 * mm});
            skCircle(sketch, "E10.0.7.23", {"center": v(0.45, -2.04) * mm, "radius": 0.09 * mm});
            skCircle(sketch, "E10.2.7.23", {"center": v(0.68, -2.17) * mm, "radius": 0.09 * mm});
            skCircle(sketch, "E10.0.7.24", {"center": v(0.45, -2.27) * mm, "radius": 0.09 * mm});
            skCircle(sketch, "E10.0.8.22", {"center": v(0.9, -1.81) * mm, "radius": 0.09 * mm});
            skCircle(sketch, "E10.2.8.22", {"center": v(1.14, -1.94) * mm, "radius": 0.09 * mm});
            skCircle(sketch, "E10.0.8.23", {"center": v(0.9, -2.04) * mm, "radius": 0.09 * mm});
            skCircle(sketch, "E10.2.8.23", {"center": v(1.14, -2.17) * mm, "radius": 0.09 * mm});
            skCircle(sketch, "E10.0.8.24", {"center": v(0.9, -2.27) * mm, "radius": 0.09 * mm});
            skCircle(sketch, "E10.0.9.22", {"center": v(1.36, -1.81) * mm, "radius": 0.09 * mm});
            skCircle(sketch, "E10.0.9.23", {"center": v(1.36, -2.04) * mm, "radius": 0.09 * mm});
            skCircle(sketch, "E11.0", {"center": v(0, 0) * mm, "radius": 2.5 * mm, "construction": true});
            skSolve(sketch);
        }
        {
            var Q0;
            Q0=qSketchRegion(id+"F3",true);
            extrude(context, id + "F4", {"entities" : qUnion([Q0]), "operationType" : NewBodyOperationType.REMOVE, "endBound" : BoundingType.THROUGH_ALL, "oppositeDirection" : true, "depth" : 25 * mm});
        }
        {
            var Q0;
            Q0=makeQuery(id+"F1.opExtrude","CAP_FACE",FACE,{"disambiguationData":[OSD([sQuery(id+"F0.wireOp",EDGE,"E1"),sQuery(id+"F0.wireOp",EDGE,"E4"),sQuery(id+"F0.wireOp",EDGE,"E5"),sQuery(id+"F0.wireOp",EDGE,"E6.1.0"),sQuery(id+"F0.wireOp",EDGE,"E6.1.1"),sQuery(id+"F0.wireOp",EDGE,"E6.2.0"),sQuery(id+"F0.wireOp",EDGE,"E6.2.1"),sQuery(id+"F0.wireOp",EDGE,"E6.3.0"),sQuery(id+"F0.wireOp",EDGE,"E6.3.1"),sQuery(id+"F0.wireOp",EDGE,"E6.4.0"),sQuery(id+"F0.wireOp",EDGE,"E6.4.1"),sQuery(id+"F0.wireOp",EDGE,"E6.5.0"),sQuery(id+"F0.wireOp",EDGE,"E6.5.1"),sQuery(id+"F0.wireOp",EDGE,"E6.6.0"),sQuery(id+"F0.wireOp",EDGE,"E6.6.1"),sQuery(id+"F0.wireOp",EDGE,"E6.7.0"),sQuery(id+"F0.wireOp",EDGE,"E6.7.1"),sQuery(id+"F0.wireOp",EDGE,"E6.8.0"),sQuery(id+"F0.wireOp",EDGE,"E6.8.1"),sQuery(id+"F0.wireOp",EDGE,"E6.9.0"),sQuery(id+"F0.wireOp",EDGE,"E6.9.1")])],"isStart":false});
            var sketch = newSketch(context, id + "F5", { "sketchPlane" : qUnion([Q0])});
            skLineSegment(sketch, "E12.bottom", {"start": v(-4.93, -4.16) * mm, "end": v(4.96, -4.16) * mm});
            skLineSegment(sketch, "E12.top", {"start": v(-4.93, 0) * mm, "end": v(4.96, 0) * mm});
            skLineSegment(sketch, "E12.left", {"start": v(-4.93, -4.16) * mm, "end": v(-4.93, 0) * mm});
            skLineSegment(sketch, "E12.right", {"start": v(4.96, -4.16) * mm, "end": v(4.96, 0) * mm});
            skSolve(sketch);
        }
        {
            var Q0;
            Q0 = qSketchRegion(id + "F5", true);
            extrude(context, id + "F6", {"entities" : qUnion([Q0]), "operationType" : NewBodyOperationType.REMOVE, "oppositeDirection" : true, "depth" : 25 * mm});
        }
    });
